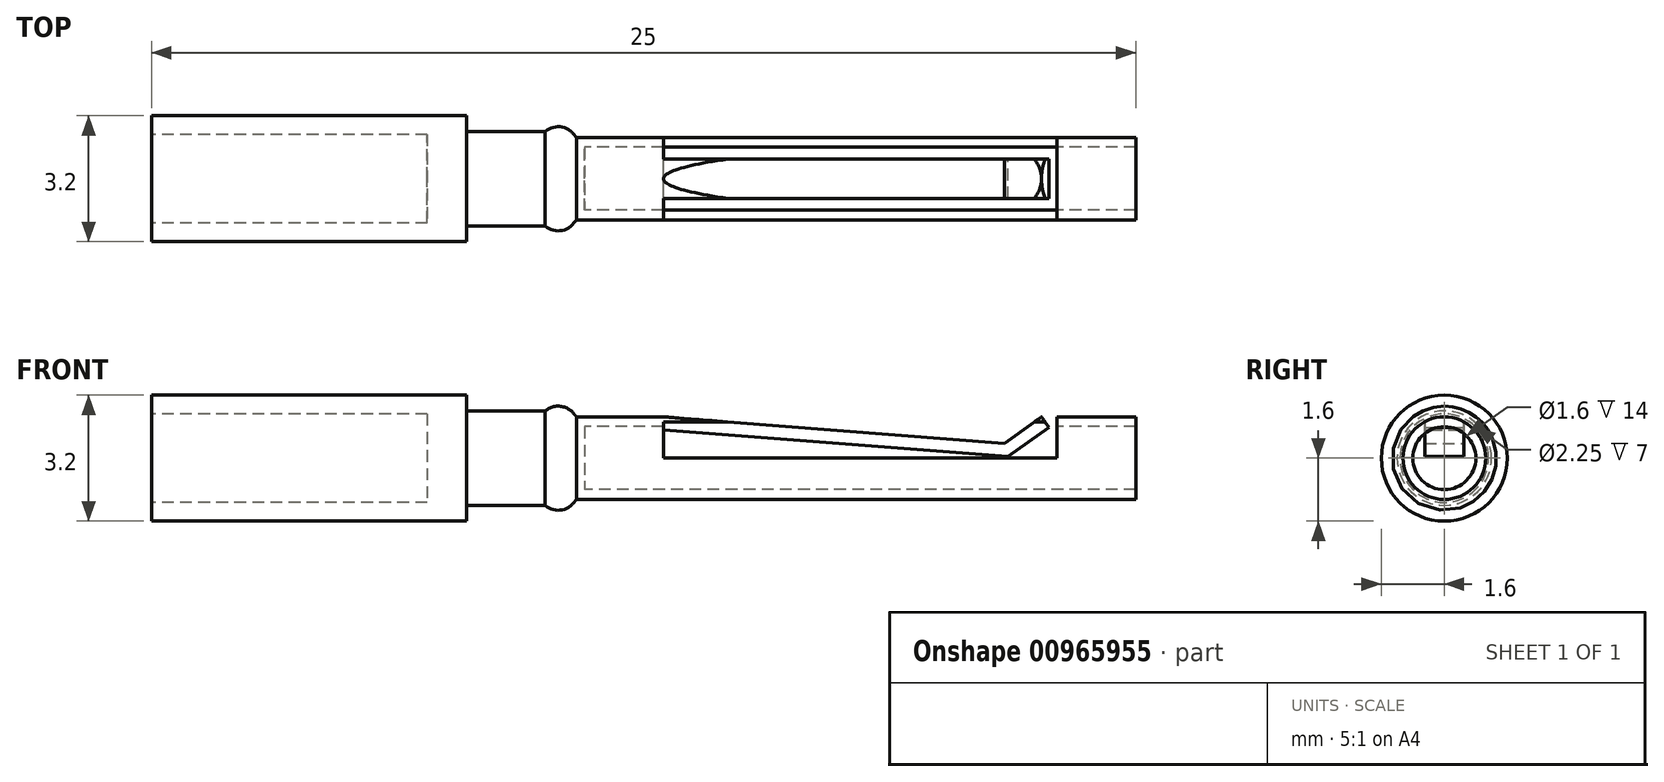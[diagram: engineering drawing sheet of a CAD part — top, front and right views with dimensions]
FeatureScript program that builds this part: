
annotation { "Feature Type Name" : "Feature", "Feature Type Description" : "" }
export const myFeature = defineFeature(function(context is Context, id is Id, definition is map)
    precondition{}
    {
        {
            var Q0;
            Q0=qCreatedBy(makeId("Top.planeOp"),FACE);
            var sketch = newSketch(context, id + "F0", { "sketchPlane" : qUnion([Q0])});
            skLineSegment(sketch, "E0", {"start": v(0, 0) * mm, "end": v(11, 0) * mm, "construction": true});
            skLineSegment(sketch, "E1", {"start": v(25, -0.8) * mm, "end": v(11, -0.8) * mm});
            skLineSegment(sketch, "E2", {"start": v(10.8, -1.05) * mm, "end": v(10, -2) * mm});
            skLineSegment(sketch, "E3", {"start": v(0, -1.6) * mm, "end": v(0, 0) * mm});
            skLineSegment(sketch, "E4", {"start": v(10, -2) * mm, "end": v(10, -1.2) * mm});
            skLineSegment(sketch, "E5", {"start": v(0, 0) * mm, "end": v(11, 0) * mm});
            skLineSegment(sketch, "E6", {"start": v(10, -1.2) * mm, "end": v(8, -1.2) * mm});
            skLineSegment(sketch, "E7", {"start": v(8, -1.2) * mm, "end": v(8, -1.6) * mm});
            skPoint(sketch, "E8.orphan", {"position": v(10, -1.6) * mm});
            skLineSegment(sketch, "E9", {"start": v(8, -1.6) * mm, "end": v(0, -1.6) * mm});
            skLineSegment(sketch, "E10", {"start": v(11, -0.8) * mm, "end": v(11, 0) * mm, "construction": true});
            skPoint(sketch, "E11.start.orphan", {"position": v(25, 0) * mm});
            skLineSegment(sketch, "E12", {"start": v(25, -1.05) * mm, "end": v(10.8, -1.05) * mm});
            skLineSegment(sketch, "E13", {"start": v(11, -0.8) * mm, "end": v(11, 0) * mm});
            skLineSegment(sketch, "E14", {"start": v(11, 0) * mm, "end": v(11, 0) * mm});
            skLineSegment(sketch, "E15", {"start": v(25, -0.8) * mm, "end": v(25, -1.05) * mm});
            skSolve(sketch);
        }
        {
            var Q0;
            Q0=makeQuery(id+"F0.imprint","IMPRINT",FACE,{"disambiguationData":[TD([[makeQuery(id+"F0.imprint","IMPRINT",EDGE,{"derivedFrom":sQuery(id+"F0.wireOp",EDGE,"E1")}),1.0]])]});
            var Q1;
            Q1=sQuery(id+"F0.wireOp",EDGE,"E5");
            revolve(context, id + "F1", {"surfaceOperationType" : NewSurfaceOperationType.NEW, "entities" : qUnion([Q0]), "axis" : qUnion([Q1]), "revolveType" : RevolveType.FULL});
        }
        {
            var Q0;
            Q0=makeQuery(id+"F1.opRevolve","SWEPT_EDGE",EDGE,{"disambiguationData":[OSD([sQuery(id+"F0.wireOp",EDGE,"E2"),sQuery(id+"F0.wireOp",EDGE,"E4")])]});
            fillet(context, id + "F2", {"entities" : qUnion([Q0]), "radius" : .5 * mm, "tangentPropagation" : true, "allowEdgeOverflow" : false});
        }
        {
            var Q0;
            Q0=makeQuery(id+"F1.opRevolve","SWEPT_FACE",FACE,{"disambiguationData":[OSD([sQuery(id+"F0.wireOp",EDGE,"E3")])]});
            var sketch = newSketch(context, id + "F3", { "sketchPlane" : qUnion([Q0])});
            skCircle(sketch, "E16", {"center": v(0, 0) * mm, "radius": 1.13 * mm});
            skSolve(sketch);
        }
        {
            var Q0;
            Q0=makeQuery(id+"F3.imprint","IMPRINT",FACE,{"disambiguationData":[TD([[makeQuery(id+"F3.imprint","IMPRINT",EDGE,{"derivedFrom":sQuery(id+"F3.wireOp",EDGE,"E16")}),1.0]])]});
            extrude(context, id + "F4", {"entities" : qUnion([Q0]), "operationType" : NewBodyOperationType.REMOVE, "oppositeDirection" : true, "depth" : 7 * mm, "offsetDistance" : 25 * mm});
        }
        {
            var Q0;
            Q0=qCreatedBy(makeId("Front.planeOp"),FACE);
            var sketch = newSketch(context, id + "F5", { "sketchPlane" : qUnion([Q0])});
            skLineSegment(sketch, "E17.bottom", {"start": v(23, 3) * mm, "end": v(13, 3) * mm});
            skLineSegment(sketch, "E17.top", {"start": v(23, 0) * mm, "end": v(13, 0) * mm});
            skLineSegment(sketch, "E17.left", {"start": v(23, 3) * mm, "end": v(23, 0) * mm});
            skLineSegment(sketch, "E17.right", {"start": v(13, 3) * mm, "end": v(13, 0) * mm});
            skSolve(sketch);
        }
        {
            var Q0;
            Q0=makeQuery(id+"F5.imprint","IMPRINT",FACE,{"disambiguationData":[TD([[makeQuery(id+"F5.imprint","IMPRINT",EDGE,{"derivedFrom":sQuery(id+"F5.wireOp",EDGE,"E17.bottom")}),1.0]])]});
            extrude(context, id + "F6", {"entities" : qUnion([Q0]), "operationType" : NewBodyOperationType.REMOVE, "oppositeDirection" : true, "depth" : 25 * mm, "offsetDistance" : 25 * mm, "hasSecondDirection" : true, "secondDirectionOppositeDirection" : false, "secondDirectionDepth" : 25 * mm});
        }
        {
            var Q0;
            Q0=qCreatedBy(makeId("Front.planeOp"),FACE);
            var sketch = newSketch(context, id + "F7", { "sketchPlane" : qUnion([Q0])});
            skLineSegment(sketch, "E18.0", {"start": v(23, 0) * mm, "end": v(13, 0) * mm, "construction": true});
            skPoint(sketch, "E18.1", {"position": v(13, 1.05) * mm});
            skLineSegment(sketch, "E19", {"start": v(13, 1.05) * mm, "end": v(21.66, 0.38) * mm});
            skLineSegment(sketch, "E20", {"start": v(21.66, 0.38) * mm, "end": v(22.6, 1.05) * mm});
            skLineSegment(sketch, "E21", {"start": v(22.6, 1.05) * mm, "end": v(22.8, 0.78) * mm});
            skLineSegment(sketch, "E22", {"start": v(22.8, 0.78) * mm, "end": v(21.75, 0.04) * mm});
            skLineSegment(sketch, "E23", {"start": v(21.75, 0.04) * mm, "end": v(13, 0.72) * mm});
            skLineSegment(sketch, "E24", {"start": v(13, 0.72) * mm, "end": v(13, 1.05) * mm});
            skSolve(sketch);
        }
        {
            var Q0;
            Q0=makeQuery(id+"F7.imprint","IMPRINT",FACE,{"disambiguationData":[TD([[makeQuery(id+"F7.imprint","IMPRINT",EDGE,{"derivedFrom":sQuery(id+"F7.wireOp",EDGE,"E19")}),-1.0]])]});
            extrude(context, id + "F8", {"entities" : qUnion([Q0]), "operationType" : NewBodyOperationType.ADD, "depth" : .5 * mm, "offsetDistance" : 25 * mm, "hasSecondDirection" : true, "secondDirectionOppositeDirection" : true, "secondDirectionDepth" : .5 * mm});
        }
        {
            var Q0;
            Q0=makeQuery(id+"F1.opRevolve","SWEPT_FACE",FACE,{"disambiguationData":[OSD([sQuery(id+"F0.wireOp",EDGE,"E15")])]});
            var sketch = newSketch(context, id + "F9", { "sketchPlane" : qUnion([Q0])});
            skCircle(sketch, "E25.0", {"center": v(0, 0) * mm, "radius": 1.05 * mm});
            skCircle(sketch, "E26", {"center": v(0, 0) * mm, "radius": 1.78 * mm});
            skSolve(sketch);
        }
        {
            var Q0;
            Q0=makeQuery(id+"F9.imprint","IMPRINT",FACE,{"disambiguationData":[TD([[makeQuery(id+"F9.imprint","IMPRINT",EDGE,{"derivedFrom":sQuery(id+"F9.wireOp",EDGE,"E25.0")}),1.0]])]});
            extrude(context, id + "F10", {"entities" : qUnion([Q0]), "operationType" : NewBodyOperationType.REMOVE, "oppositeDirection" : true, "depth" : 12.78 * mm, "offsetDistance" : 25 * mm});
        }
    });
